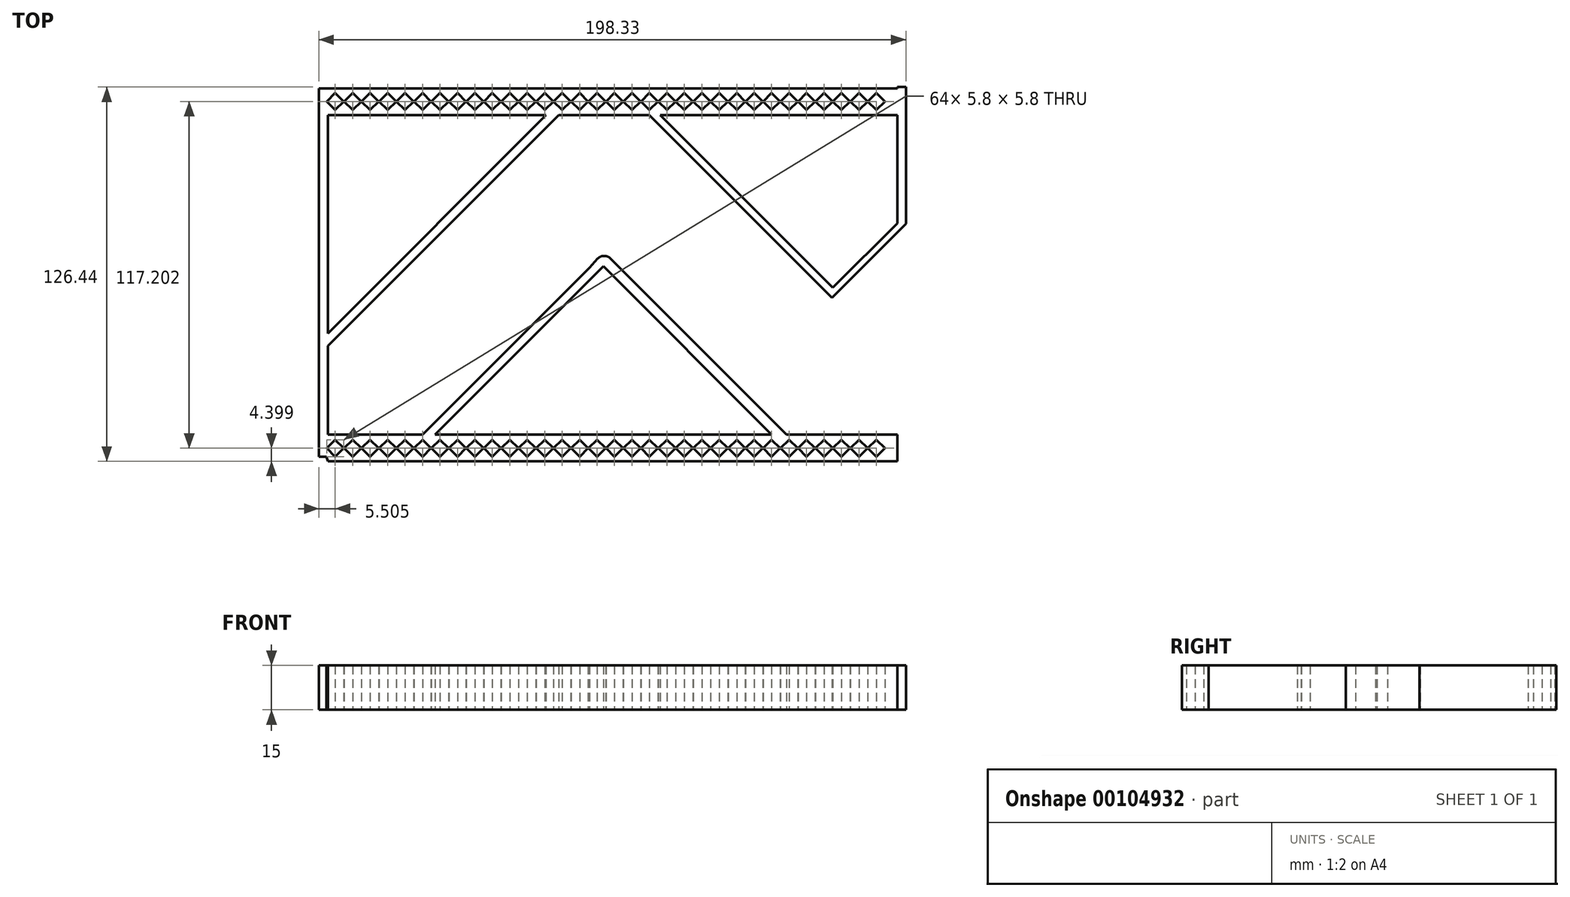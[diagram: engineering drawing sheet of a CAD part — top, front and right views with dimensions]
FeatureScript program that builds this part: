
annotation { "Feature Type Name" : "Feature", "Feature Type Description" : "" }
export const myFeature = defineFeature(function(context is Context, id is Id, definition is map)
    precondition{}
    {
        {
            var Q0;
            Q0=qCreatedBy(makeId("Top.planeOp"),FACE);
            var sketch = newSketch(context, id + "F0", { "sketchPlane" : qUnion([Q0])});
            skLineSegment(sketch, "E0", {"start": v(2.95, 0) * mm, "end": v(0.05, 2.9) * mm});
            skLineSegment(sketch, "E1", {"start": v(0.05, 2.9) * mm, "end": v(2.95, 5.8) * mm});
            skLineSegment(sketch, "E2", {"start": v(2.95, 5.8) * mm, "end": v(5.85, 2.9) * mm});
            skLineSegment(sketch, "E3", {"start": v(5.85, 2.9) * mm, "end": v(2.95, 0) * mm});
            skLineSegment(sketch, "E4", {"start": v(0, 0) * mm, "end": v(0, 5.85) * mm});
            skLineSegment(sketch, "E5.MirrorCS", {"start": v(-2.95, 0) * mm, "end": v(-0.05, 2.9) * mm});
            skLineSegment(sketch, "E6.MirrorCS", {"start": v(-0.05, 2.9) * mm, "end": v(-2.95, 5.8) * mm});
            skLineSegment(sketch, "E7.MirrorCS", {"start": v(-2.95, 5.8) * mm, "end": v(-5.85, 2.9) * mm});
            skLineSegment(sketch, "E8.MirrorCS", {"start": v(-5.85, 2.9) * mm, "end": v(-2.95, 0) * mm});
            skLineSegment(sketch, "E9", {"start": v(5.9, 0) * mm, "end": v(5.9, 5.85) * mm});
            skLineSegment(sketch, "E10", {"start": v(-5.9, 0) * mm, "end": v(-5.9, 6.46) * mm});
            skLineSegment(sketch, "E11.MirrorCS", {"start": v(5.95, 2.9) * mm, "end": v(8.85, 0) * mm});
            skLineSegment(sketch, "E12.MirrorCS", {"start": v(8.85, 5.8) * mm, "end": v(5.95, 2.9) * mm});
            skLineSegment(sketch, "E13.MirrorCS", {"start": v(11.75, 2.9) * mm, "end": v(8.85, 5.8) * mm});
            skLineSegment(sketch, "E14.MirrorCS", {"start": v(8.85, 0) * mm, "end": v(11.75, 2.9) * mm});
            skLineSegment(sketch, "E15.MirrorCS", {"start": v(14.75, 0) * mm, "end": v(11.85, 2.9) * mm});
            skLineSegment(sketch, "E16.MirrorCS", {"start": v(17.64, 2.9) * mm, "end": v(14.75, 0) * mm});
            skLineSegment(sketch, "E17.MirrorCS", {"start": v(14.75, 5.8) * mm, "end": v(17.64, 2.9) * mm});
            skLineSegment(sketch, "E18.MirrorCS", {"start": v(11.85, 2.9) * mm, "end": v(14.75, 5.8) * mm});
            skLineSegment(sketch, "E19.MirrorCS", {"start": v(17.7, 0) * mm, "end": v(17.7, 6.46) * mm});
            skLineSegment(sketch, "E20.MirrorCS", {"start": v(-5.95, 2.9) * mm, "end": v(-8.85, 0) * mm});
            skLineSegment(sketch, "E21.MirrorCS", {"start": v(-8.85, 5.8) * mm, "end": v(-5.95, 2.9) * mm});
            skLineSegment(sketch, "E22.MirrorCS", {"start": v(-11.75, 2.9) * mm, "end": v(-8.85, 5.8) * mm});
            skLineSegment(sketch, "E23.MirrorCS", {"start": v(-8.85, 0) * mm, "end": v(-11.75, 2.9) * mm});
            skLineSegment(sketch, "E24.MirrorCS", {"start": v(-11.85, 2.9) * mm, "end": v(-14.75, 5.8) * mm});
            skLineSegment(sketch, "E25.MirrorCS", {"start": v(-14.75, 5.8) * mm, "end": v(-17.64, 2.9) * mm});
            skLineSegment(sketch, "E26.MirrorCS", {"start": v(-17.64, 2.9) * mm, "end": v(-14.75, 0) * mm});
            skLineSegment(sketch, "E27.MirrorCS", {"start": v(-14.75, 0) * mm, "end": v(-11.85, 2.9) * mm});
            skLineSegment(sketch, "E28.MirrorCS", {"start": v(-20.64, 5.8) * mm, "end": v(-17.74, 2.9) * mm});
            skLineSegment(sketch, "E29.MirrorCS", {"start": v(-23.54, 2.9) * mm, "end": v(-20.64, 5.8) * mm});
            skLineSegment(sketch, "E30.MirrorCS", {"start": v(-20.64, 0) * mm, "end": v(-23.54, 2.9) * mm});
            skLineSegment(sketch, "E31.MirrorCS", {"start": v(-17.74, 2.9) * mm, "end": v(-20.64, 0) * mm});
            skLineSegment(sketch, "E32.MirrorCS", {"start": v(-23.64, 2.9) * mm, "end": v(-26.54, 5.8) * mm});
            skLineSegment(sketch, "E33.MirrorCS", {"start": v(-26.54, 5.8) * mm, "end": v(-29.44, 2.9) * mm});
            skLineSegment(sketch, "E34.MirrorCS", {"start": v(-29.44, 2.9) * mm, "end": v(-26.54, 0) * mm});
            skLineSegment(sketch, "E35.MirrorCS", {"start": v(-26.54, 0) * mm, "end": v(-23.64, 2.9) * mm});
            skLineSegment(sketch, "E36.MirrorCS", {"start": v(-29.5, 0) * mm, "end": v(-29.5, 6.46) * mm});
            skLineSegment(sketch, "E37.MirrorCS", {"start": v(20.64, 5.8) * mm, "end": v(17.74, 2.9) * mm});
            skLineSegment(sketch, "E38.MirrorCS", {"start": v(17.74, 2.9) * mm, "end": v(20.64, 0) * mm});
            skLineSegment(sketch, "E39.MirrorCS", {"start": v(20.64, 0) * mm, "end": v(23.54, 2.9) * mm});
            skLineSegment(sketch, "E40.MirrorCS", {"start": v(23.54, 2.9) * mm, "end": v(20.64, 5.8) * mm});
            skLineSegment(sketch, "E41.MirrorCS", {"start": v(23.64, 2.9) * mm, "end": v(26.54, 5.8) * mm});
            skLineSegment(sketch, "E42.MirrorCS", {"start": v(26.54, 0) * mm, "end": v(23.64, 2.9) * mm});
            skLineSegment(sketch, "E43.MirrorCS", {"start": v(29.44, 2.9) * mm, "end": v(26.54, 0) * mm});
            skLineSegment(sketch, "E44.MirrorCS", {"start": v(26.54, 5.8) * mm, "end": v(29.44, 2.9) * mm});
            skLineSegment(sketch, "E45.MirrorCS", {"start": v(29.54, 2.9) * mm, "end": v(32.44, 0) * mm});
            skLineSegment(sketch, "E46.MirrorCS", {"start": v(32.44, 0) * mm, "end": v(35.34, 2.9) * mm});
            skLineSegment(sketch, "E47.MirrorCS", {"start": v(35.34, 2.9) * mm, "end": v(32.44, 5.8) * mm});
            skLineSegment(sketch, "E48.MirrorCS", {"start": v(32.44, 5.8) * mm, "end": v(29.54, 2.9) * mm});
            skLineSegment(sketch, "E49.MirrorCS", {"start": v(38.34, 0) * mm, "end": v(35.44, 2.9) * mm});
            skLineSegment(sketch, "E50.MirrorCS", {"start": v(41.24, 2.9) * mm, "end": v(38.34, 0) * mm});
            skLineSegment(sketch, "E51.MirrorCS", {"start": v(38.34, 5.8) * mm, "end": v(41.24, 2.9) * mm});
            skLineSegment(sketch, "E52.MirrorCS", {"start": v(35.44, 2.9) * mm, "end": v(38.34, 5.8) * mm});
            skLineSegment(sketch, "E53.MirrorCS", {"start": v(41.34, 2.9) * mm, "end": v(44.24, 0) * mm});
            skLineSegment(sketch, "E54.MirrorCS", {"start": v(44.24, 0) * mm, "end": v(47.14, 2.9) * mm});
            skLineSegment(sketch, "E55.MirrorCS", {"start": v(47.14, 2.9) * mm, "end": v(44.24, 5.8) * mm});
            skLineSegment(sketch, "E56.MirrorCS", {"start": v(44.24, 5.8) * mm, "end": v(41.34, 2.9) * mm});
            skLineSegment(sketch, "E57.MirrorCS", {"start": v(50.14, 0) * mm, "end": v(47.24, 2.9) * mm});
            skLineSegment(sketch, "E58.MirrorCS", {"start": v(53.03, 2.9) * mm, "end": v(50.14, 0) * mm});
            skLineSegment(sketch, "E59.MirrorCS", {"start": v(50.14, 5.8) * mm, "end": v(53.03, 2.9) * mm});
            skLineSegment(sketch, "E60.MirrorCS", {"start": v(47.24, 2.9) * mm, "end": v(50.14, 5.8) * mm});
            skLineSegment(sketch, "E61.MirrorCS", {"start": v(53.13, 2.9) * mm, "end": v(56.03, 0) * mm});
            skLineSegment(sketch, "E62.MirrorCS", {"start": v(56.03, 0) * mm, "end": v(58.93, 2.9) * mm});
            skLineSegment(sketch, "E63.MirrorCS", {"start": v(58.93, 2.9) * mm, "end": v(56.03, 5.8) * mm});
            skLineSegment(sketch, "E64.MirrorCS", {"start": v(56.03, 5.8) * mm, "end": v(53.13, 2.9) * mm});
            skLineSegment(sketch, "E65.MirrorCS", {"start": v(61.93, 0) * mm, "end": v(59.03, 2.9) * mm});
            skLineSegment(sketch, "E66.MirrorCS", {"start": v(64.83, 2.9) * mm, "end": v(61.93, 0) * mm});
            skLineSegment(sketch, "E67.MirrorCS", {"start": v(61.93, 5.8) * mm, "end": v(64.83, 2.9) * mm});
            skLineSegment(sketch, "E68.MirrorCS", {"start": v(59.03, 2.9) * mm, "end": v(61.93, 5.8) * mm});
            skLineSegment(sketch, "E69.MirrorCS", {"start": v(64.88, 0) * mm, "end": v(64.88, 6.46) * mm});
            skLineSegment(sketch, "E70.MirrorCS", {"start": v(-32.44, 5.8) * mm, "end": v(-29.54, 2.9) * mm});
            skLineSegment(sketch, "E71.MirrorCS", {"start": v(-35.34, 2.9) * mm, "end": v(-32.44, 5.8) * mm});
            skLineSegment(sketch, "E72.MirrorCS", {"start": v(-32.44, 0) * mm, "end": v(-35.34, 2.9) * mm});
            skLineSegment(sketch, "E73.MirrorCS", {"start": v(-29.54, 2.9) * mm, "end": v(-32.44, 0) * mm});
            skLineSegment(sketch, "E74.MirrorCS", {"start": v(-35.44, 2.9) * mm, "end": v(-38.34, 5.8) * mm});
            skLineSegment(sketch, "E75.MirrorCS", {"start": v(-38.34, 5.8) * mm, "end": v(-41.24, 2.9) * mm});
            skLineSegment(sketch, "E76.MirrorCS", {"start": v(-38.34, 0) * mm, "end": v(-35.44, 2.9) * mm});
            skLineSegment(sketch, "E77.MirrorCS", {"start": v(-41.24, 2.9) * mm, "end": v(-38.34, 0) * mm});
            skLineSegment(sketch, "E78.MirrorCS", {"start": v(-44.24, 5.8) * mm, "end": v(-41.34, 2.9) * mm});
            skLineSegment(sketch, "E79.MirrorCS", {"start": v(-47.14, 2.9) * mm, "end": v(-44.24, 5.8) * mm});
            skLineSegment(sketch, "E80.MirrorCS", {"start": v(-44.24, 0) * mm, "end": v(-47.14, 2.9) * mm});
            skLineSegment(sketch, "E81.MirrorCS", {"start": v(-41.34, 2.9) * mm, "end": v(-44.24, 0) * mm});
            skLineSegment(sketch, "E82.MirrorCS", {"start": v(-47.24, 2.9) * mm, "end": v(-50.14, 5.8) * mm});
            skLineSegment(sketch, "E83.MirrorCS", {"start": v(-50.14, 5.8) * mm, "end": v(-53.03, 2.9) * mm});
            skLineSegment(sketch, "E84.MirrorCS", {"start": v(-53.03, 2.9) * mm, "end": v(-50.14, 0) * mm});
            skLineSegment(sketch, "E85.MirrorCS", {"start": v(-50.14, 0) * mm, "end": v(-47.24, 2.9) * mm});
            skLineSegment(sketch, "E86.MirrorCS", {"start": v(-56.03, 5.8) * mm, "end": v(-53.13, 2.9) * mm});
            skLineSegment(sketch, "E87.MirrorCS", {"start": v(-58.93, 2.9) * mm, "end": v(-56.03, 5.8) * mm});
            skLineSegment(sketch, "E88.MirrorCS", {"start": v(-56.03, 0) * mm, "end": v(-58.93, 2.9) * mm});
            skLineSegment(sketch, "E89.MirrorCS", {"start": v(-53.13, 2.9) * mm, "end": v(-56.03, 0) * mm});
            skLineSegment(sketch, "E90.MirrorCS", {"start": v(-59.03, 2.9) * mm, "end": v(-61.93, 5.8) * mm});
            skLineSegment(sketch, "E91.MirrorCS", {"start": v(-61.93, 5.8) * mm, "end": v(-64.83, 2.9) * mm});
            skLineSegment(sketch, "E92.MirrorCS", {"start": v(-64.83, 2.9) * mm, "end": v(-61.93, 0) * mm});
            skLineSegment(sketch, "E93.MirrorCS", {"start": v(-61.93, 0) * mm, "end": v(-59.03, 2.9) * mm});
            skLineSegment(sketch, "E94.MirrorCS", {"start": v(-67.83, 5.8) * mm, "end": v(-64.93, 2.9) * mm});
            skLineSegment(sketch, "E95.MirrorCS", {"start": v(-70.73, 2.9) * mm, "end": v(-67.83, 5.8) * mm});
            skLineSegment(sketch, "E96.MirrorCS", {"start": v(-67.83, 0) * mm, "end": v(-70.73, 2.9) * mm});
            skLineSegment(sketch, "E97.MirrorCS", {"start": v(-64.93, 2.9) * mm, "end": v(-67.83, 0) * mm});
            skLineSegment(sketch, "E98.MirrorCS", {"start": v(-70.83, 2.9) * mm, "end": v(-73.73, 5.8) * mm});
            skLineSegment(sketch, "E99.MirrorCS", {"start": v(-73.73, 5.8) * mm, "end": v(-76.63, 2.9) * mm});
            skLineSegment(sketch, "E100.MirrorCS", {"start": v(-76.63, 2.9) * mm, "end": v(-73.73, 0) * mm});
            skLineSegment(sketch, "E101.MirrorCS", {"start": v(-73.73, 0) * mm, "end": v(-70.83, 2.9) * mm});
            skLineSegment(sketch, "E102.MirrorCS", {"start": v(-79.63, 5.8) * mm, "end": v(-76.73, 2.9) * mm});
            skLineSegment(sketch, "E103.MirrorCS", {"start": v(-82.53, 2.9) * mm, "end": v(-79.63, 5.8) * mm});
            skLineSegment(sketch, "E104.MirrorCS", {"start": v(-79.63, 0) * mm, "end": v(-82.53, 2.9) * mm});
            skLineSegment(sketch, "E105.MirrorCS", {"start": v(-76.73, 2.9) * mm, "end": v(-79.63, 0) * mm});
            skLineSegment(sketch, "E106.MirrorCS", {"start": v(-82.63, 2.9) * mm, "end": v(-85.52, 5.8) * mm});
            skLineSegment(sketch, "E107.MirrorCS", {"start": v(-85.52, 5.8) * mm, "end": v(-88.42, 2.9) * mm});
            skLineSegment(sketch, "E108.MirrorCS", {"start": v(-88.42, 2.9) * mm, "end": v(-85.52, 0) * mm});
            skLineSegment(sketch, "E109.MirrorCS", {"start": v(-85.52, 0) * mm, "end": v(-82.63, 2.9) * mm});
            skLineSegment(sketch, "E110.MirrorCS", {"start": v(-91.42, 5.8) * mm, "end": v(-88.52, 2.9) * mm});
            skLineSegment(sketch, "E111.MirrorCS", {"start": v(-94.32, 2.9) * mm, "end": v(-91.42, 5.8) * mm});
            skLineSegment(sketch, "E112.MirrorCS", {"start": v(-91.42, 0) * mm, "end": v(-94.32, 2.9) * mm});
            skLineSegment(sketch, "E113.MirrorCS", {"start": v(-88.52, 2.9) * mm, "end": v(-91.42, 0) * mm});
            skLineSegment(sketch, "E114.MirrorCS", {"start": v(-94.42, 2.9) * mm, "end": v(-97.32, 5.8) * mm});
            skLineSegment(sketch, "E115.MirrorCS", {"start": v(-97.32, 5.8) * mm, "end": v(-100.22, 2.9) * mm});
            skLineSegment(sketch, "E116.MirrorCS", {"start": v(-100.22, 2.9) * mm, "end": v(-97.32, 0) * mm});
            skLineSegment(sketch, "E117.MirrorCS", {"start": v(-97.32, 0) * mm, "end": v(-94.42, 2.9) * mm});
            skLineSegment(sketch, "E118.MirrorCS", {"start": v(-115.02, 5.8) * mm, "end": v(-112.12, 2.9) * mm});
            skLineSegment(sketch, "E119.MirrorCS", {"start": v(-120.91, 0) * mm, "end": v(-118.02, 2.9) * mm});
            skLineSegment(sketch, "E120.MirrorCS", {"start": v(-106.12, 2.9) * mm, "end": v(-103.22, 5.8) * mm});
            skLineSegment(sketch, "E121.MirrorCS", {"start": v(-117.92, 2.9) * mm, "end": v(-115.02, 5.8) * mm});
            skLineSegment(sketch, "E122.MirrorCS", {"start": v(-109.12, 0) * mm, "end": v(-106.22, 2.9) * mm});
            skLineSegment(sketch, "E123.MirrorCS", {"start": v(-123.81, 2.9) * mm, "end": v(-120.91, 0) * mm});
            skLineSegment(sketch, "E124.MirrorCS", {"start": v(-103.22, 0) * mm, "end": v(-106.12, 2.9) * mm});
            skLineSegment(sketch, "E125.MirrorCS", {"start": v(-109.12, 5.8) * mm, "end": v(-112.02, 2.9) * mm});
            skLineSegment(sketch, "E126.MirrorCS", {"start": v(-115.02, 0) * mm, "end": v(-117.92, 2.9) * mm});
            skLineSegment(sketch, "E127.MirrorCS", {"start": v(-118.02, 2.9) * mm, "end": v(-120.91, 5.8) * mm});
            skLineSegment(sketch, "E128.MirrorCS", {"start": v(-123.86, 0) * mm, "end": v(-123.86, 6.46) * mm});
            skLineSegment(sketch, "E129.MirrorCS", {"start": v(-112.12, 2.9) * mm, "end": v(-115.02, 0) * mm});
            skLineSegment(sketch, "E130.MirrorCS", {"start": v(-120.91, 5.8) * mm, "end": v(-123.81, 2.9) * mm});
            skLineSegment(sketch, "E131.MirrorCS", {"start": v(-106.22, 2.9) * mm, "end": v(-109.12, 5.8) * mm});
            skLineSegment(sketch, "E132.MirrorCS", {"start": v(-112.02, 2.9) * mm, "end": v(-109.12, 0) * mm});
            skLineSegment(sketch, "E133.MirrorCS", {"start": v(-76.68, 0) * mm, "end": v(-76.68, 6.46) * mm});
            skLineSegment(sketch, "E134.MirrorCS", {"start": v(-100.32, 2.9) * mm, "end": v(-103.22, 0) * mm});
            skLineSegment(sketch, "E135.MirrorCS", {"start": v(-103.22, 5.8) * mm, "end": v(-100.32, 2.9) * mm});
            skLineSegment(sketch, "E136.bottom", {"start": v(-123.42, -1.5) * mm, "end": v(68.98, -1.5) * mm});
            skLineSegment(sketch, "E136.top", {"start": v(-123.42, 7.5) * mm, "end": v(68.98, 7.5) * mm});
            skLineSegment(sketch, "E136.right", {"start": v(68.98, -1.5) * mm, "end": v(68.98, 7.5) * mm});
            skCircle(sketch, "E137", {"center": v(-103.92, 28.34) * mm, "radius": 19 * mm});
            skLineSegment(sketch, "E138", {"start": v(-123.42, 7.5) * mm, "end": v(-123.42, 37.5) * mm});
            skLineSegment(sketch, "E139", {"start": v(-123.42, 37.5) * mm, "end": v(-45.42, 115.5) * mm});
            skLineSegment(sketch, "E140", {"start": v(-139.2, 61.5) * mm, "end": v(93.37, 61.5) * mm, "construction": true});
            skLineSegment(sketch, "E141.MirrorCS", {"start": v(-82.63, 120.1) * mm, "end": v(-85.52, 117.2) * mm});
            skLineSegment(sketch, "E142.MirrorCS", {"start": v(-88.42, 120.1) * mm, "end": v(-85.52, 123) * mm});
            skLineSegment(sketch, "E143.MirrorCS", {"start": v(-85.52, 117.2) * mm, "end": v(-88.42, 120.1) * mm});
            skLineSegment(sketch, "E144.MirrorCS", {"start": v(-85.52, 123) * mm, "end": v(-82.63, 120.1) * mm});
            skLineSegment(sketch, "E145.MirrorCS", {"start": v(-91.42, 117.2) * mm, "end": v(-88.52, 120.1) * mm});
            skLineSegment(sketch, "E146.MirrorCS", {"start": v(-88.52, 120.1) * mm, "end": v(-91.42, 123) * mm});
            skLineSegment(sketch, "E147.MirrorCS", {"start": v(-79.63, 123) * mm, "end": v(-82.53, 120.1) * mm});
            skLineSegment(sketch, "E148.MirrorCS", {"start": v(-82.53, 120.1) * mm, "end": v(-79.63, 117.2) * mm});
            skLineSegment(sketch, "E149.MirrorCS", {"start": v(-94.32, 120.1) * mm, "end": v(-91.42, 117.2) * mm});
            skLineSegment(sketch, "E150.MirrorCS", {"start": v(-97.32, 123) * mm, "end": v(-94.42, 120.1) * mm});
            skLineSegment(sketch, "E151.MirrorCS", {"start": v(-115.02, 123) * mm, "end": v(-117.92, 120.1) * mm});
            skLineSegment(sketch, "E152.MirrorCS", {"start": v(-120.91, 123) * mm, "end": v(-118.02, 120.1) * mm});
            skLineSegment(sketch, "E153.MirrorCS", {"start": v(-118.02, 120.1) * mm, "end": v(-120.91, 117.2) * mm});
            skLineSegment(sketch, "E154.MirrorCS", {"start": v(-91.42, 123) * mm, "end": v(-94.32, 120.1) * mm});
            skLineSegment(sketch, "E155.MirrorCS", {"start": v(-117.92, 120.1) * mm, "end": v(-115.02, 117.2) * mm});
            skLineSegment(sketch, "E156.MirrorCS", {"start": v(-94.42, 120.1) * mm, "end": v(-97.32, 117.2) * mm});
            skLineSegment(sketch, "E157.MirrorCS", {"start": v(-109.12, 117.2) * mm, "end": v(-112.02, 120.1) * mm});
            skLineSegment(sketch, "E158.MirrorCS", {"start": v(-112.02, 120.1) * mm, "end": v(-109.12, 123) * mm});
            skLineSegment(sketch, "E159.MirrorCS", {"start": v(-109.12, 123) * mm, "end": v(-106.22, 120.1) * mm});
            skLineSegment(sketch, "E160.MirrorCS", {"start": v(-115.02, 117.2) * mm, "end": v(-112.12, 120.1) * mm});
            skLineSegment(sketch, "E161.MirrorCS", {"start": v(-103.22, 123) * mm, "end": v(-106.12, 120.1) * mm});
            skLineSegment(sketch, "E162.MirrorCS", {"start": v(-106.12, 120.1) * mm, "end": v(-103.22, 117.2) * mm});
            skLineSegment(sketch, "E163.MirrorCS", {"start": v(-106.22, 120.1) * mm, "end": v(-109.12, 117.2) * mm});
            skLineSegment(sketch, "E164.MirrorCS", {"start": v(-112.12, 120.1) * mm, "end": v(-115.02, 123) * mm});
            skLineSegment(sketch, "E165.MirrorCS", {"start": v(-97.32, 117.2) * mm, "end": v(-100.22, 120.1) * mm});
            skLineSegment(sketch, "E166.MirrorCS", {"start": v(-76.73, 120.1) * mm, "end": v(-79.63, 123) * mm});
            skLineSegment(sketch, "E167.MirrorCS", {"start": v(-100.22, 120.1) * mm, "end": v(-97.32, 123) * mm});
            skLineSegment(sketch, "E168.MirrorCS", {"start": v(-79.63, 117.2) * mm, "end": v(-76.73, 120.1) * mm});
            skLineSegment(sketch, "E169.MirrorCS", {"start": v(-123.81, 120.1) * mm, "end": v(-120.91, 123) * mm});
            skLineSegment(sketch, "E170.MirrorCS", {"start": v(-73.73, 117.2) * mm, "end": v(-76.63, 120.1) * mm});
            skLineSegment(sketch, "E171.MirrorCS", {"start": v(-100.32, 120.1) * mm, "end": v(-103.22, 123) * mm});
            skLineSegment(sketch, "E172.MirrorCS", {"start": v(38.34, 123) * mm, "end": v(35.44, 120.1) * mm});
            skLineSegment(sketch, "E173.MirrorCS", {"start": v(-76.63, 120.1) * mm, "end": v(-73.73, 123) * mm});
            skLineSegment(sketch, "E174.MirrorCS", {"start": v(-103.22, 117.2) * mm, "end": v(-100.32, 120.1) * mm});
            skLineSegment(sketch, "E175.MirrorCS", {"start": v(-120.91, 117.2) * mm, "end": v(-123.81, 120.1) * mm});
            skLineSegment(sketch, "E176.MirrorCS", {"start": v(-76.68, 123) * mm, "end": v(-76.68, 116.54) * mm});
            skLineSegment(sketch, "E177.MirrorCS", {"start": v(23.64, 120.1) * mm, "end": v(26.54, 117.2) * mm});
            skLineSegment(sketch, "E178.MirrorCS", {"start": v(-26.54, 117.2) * mm, "end": v(-29.44, 120.1) * mm});
            skLineSegment(sketch, "E179.MirrorCS", {"start": v(35.34, 120.1) * mm, "end": v(32.44, 117.2) * mm});
            skLineSegment(sketch, "E180.MirrorCS", {"start": v(32.44, 117.2) * mm, "end": v(29.54, 120.1) * mm});
            skLineSegment(sketch, "E181.MirrorCS", {"start": v(8.85, 117.2) * mm, "end": v(5.95, 120.1) * mm});
            skLineSegment(sketch, "E182.MirrorCS", {"start": v(5.95, 120.1) * mm, "end": v(8.85, 123) * mm});
            skLineSegment(sketch, "E183.MirrorCS", {"start": v(-29.5, 123) * mm, "end": v(-29.5, 116.54) * mm});
            skLineSegment(sketch, "E184.MirrorCS", {"start": v(-70.83, 120.1) * mm, "end": v(-73.73, 117.2) * mm});
            skLineSegment(sketch, "E185.MirrorCS", {"start": v(11.85, 120.1) * mm, "end": v(14.75, 117.2) * mm});
            skLineSegment(sketch, "E186.MirrorCS", {"start": v(5.9, 123) * mm, "end": v(5.9, 117.15) * mm});
            skLineSegment(sketch, "E187.MirrorCS", {"start": v(-2.95, 117.2) * mm, "end": v(-5.85, 120.1) * mm});
            skLineSegment(sketch, "E188.MirrorCS", {"start": v(35.44, 120.1) * mm, "end": v(38.34, 117.2) * mm});
            skLineSegment(sketch, "E189.MirrorCS", {"start": v(-0.05, 120.1) * mm, "end": v(-2.95, 117.2) * mm});
            skLineSegment(sketch, "E190.MirrorCS", {"start": v(-2.95, 123) * mm, "end": v(-0.05, 120.1) * mm});
            skLineSegment(sketch, "E191.MirrorCS", {"start": v(0, 123) * mm, "end": v(0, 117.15) * mm});
            skLineSegment(sketch, "E192.MirrorCS", {"start": v(-29.54, 120.1) * mm, "end": v(-32.44, 123) * mm});
            skLineSegment(sketch, "E193.MirrorCS", {"start": v(5.85, 120.1) * mm, "end": v(2.95, 123) * mm});
            skLineSegment(sketch, "E194.MirrorCS", {"start": v(2.95, 117.2) * mm, "end": v(5.85, 120.1) * mm});
            skLineSegment(sketch, "E195.MirrorCS", {"start": v(0.05, 120.1) * mm, "end": v(2.95, 117.2) * mm});
            skLineSegment(sketch, "E196.MirrorCS", {"start": v(29.44, 120.1) * mm, "end": v(26.54, 123) * mm});
            skLineSegment(sketch, "E197.MirrorCS", {"start": v(2.95, 123) * mm, "end": v(0.05, 120.1) * mm});
            skLineSegment(sketch, "E198.MirrorCS", {"start": v(14.75, 123) * mm, "end": v(11.85, 120.1) * mm});
            skLineSegment(sketch, "E199.MirrorCS", {"start": v(8.85, 123) * mm, "end": v(11.75, 120.1) * mm});
            skLineSegment(sketch, "E200.MirrorCS", {"start": v(11.75, 120.1) * mm, "end": v(8.85, 117.2) * mm});
            skLineSegment(sketch, "E201.MirrorCS", {"start": v(26.54, 117.2) * mm, "end": v(29.44, 120.1) * mm});
            skLineSegment(sketch, "E202.MirrorCS", {"start": v(-123.86, 123) * mm, "end": v(-123.86, 116.54) * mm});
            skLineSegment(sketch, "E203.MirrorCS", {"start": v(32.44, 123) * mm, "end": v(35.34, 120.1) * mm});
            skLineSegment(sketch, "E204.MirrorCS", {"start": v(29.54, 120.1) * mm, "end": v(32.44, 123) * mm});
            skLineSegment(sketch, "E205.MirrorCS", {"start": v(20.64, 123) * mm, "end": v(23.54, 120.1) * mm});
            skLineSegment(sketch, "E206.MirrorCS", {"start": v(-29.44, 120.1) * mm, "end": v(-26.54, 123) * mm});
            skLineSegment(sketch, "E207.MirrorCS", {"start": v(-32.44, 117.2) * mm, "end": v(-29.54, 120.1) * mm});
            skLineSegment(sketch, "E208.MirrorCS", {"start": v(23.54, 120.1) * mm, "end": v(20.64, 117.2) * mm});
            skLineSegment(sketch, "E209.MirrorCS", {"start": v(-73.73, 123) * mm, "end": v(-70.83, 120.1) * mm});
            skLineSegment(sketch, "E210.MirrorCS", {"start": v(26.54, 123) * mm, "end": v(23.64, 120.1) * mm});
            skLineSegment(sketch, "E211.MirrorCS", {"start": v(-67.83, 123) * mm, "end": v(-70.73, 120.1) * mm});
            skLineSegment(sketch, "E212.MirrorCS", {"start": v(56.03, 117.2) * mm, "end": v(53.13, 120.1) * mm});
            skLineSegment(sketch, "E213.MirrorCS", {"start": v(-44.24, 123) * mm, "end": v(-47.14, 120.1) * mm});
            skLineSegment(sketch, "E214.MirrorCS", {"start": v(-70.73, 120.1) * mm, "end": v(-67.83, 117.2) * mm});
            skLineSegment(sketch, "E215.MirrorCS", {"start": v(17.7, 123) * mm, "end": v(17.7, 116.54) * mm});
            skLineSegment(sketch, "E216.MirrorCS", {"start": v(-41.34, 120.1) * mm, "end": v(-44.24, 123) * mm});
            skLineSegment(sketch, "E217.MirrorCS", {"start": v(61.93, 123) * mm, "end": v(59.03, 120.1) * mm});
            skLineSegment(sketch, "E218.MirrorCS", {"start": v(41.24, 120.1) * mm, "end": v(38.34, 123) * mm});
            skLineSegment(sketch, "E219.MirrorCS", {"start": v(-26.54, 123) * mm, "end": v(-23.64, 120.1) * mm});
            skLineSegment(sketch, "E220.MirrorCS", {"start": v(-64.93, 120.1) * mm, "end": v(-67.83, 123) * mm});
            skLineSegment(sketch, "E221.MirrorCS", {"start": v(-23.64, 120.1) * mm, "end": v(-26.54, 117.2) * mm});
            skLineSegment(sketch, "E222.MirrorCS", {"start": v(56.03, 123) * mm, "end": v(58.93, 120.1) * mm});
            skLineSegment(sketch, "E223.MirrorCS", {"start": v(-44.24, 117.2) * mm, "end": v(-41.34, 120.1) * mm});
            skLineSegment(sketch, "E224.MirrorCS", {"start": v(17.64, 120.1) * mm, "end": v(14.75, 123) * mm});
            skLineSegment(sketch, "E225.MirrorCS", {"start": v(58.93, 120.1) * mm, "end": v(56.03, 117.2) * mm});
            skLineSegment(sketch, "E226.MirrorCS", {"start": v(-67.83, 117.2) * mm, "end": v(-64.93, 120.1) * mm});
            skLineSegment(sketch, "E227.MirrorCS", {"start": v(-5.95, 120.1) * mm, "end": v(-8.85, 123) * mm});
            skLineSegment(sketch, "E228.MirrorCS", {"start": v(-47.24, 120.1) * mm, "end": v(-50.14, 117.2) * mm});
            skLineSegment(sketch, "E229.MirrorCS", {"start": v(64.83, 120.1) * mm, "end": v(61.93, 123) * mm});
            skLineSegment(sketch, "E230.MirrorCS", {"start": v(38.34, 117.2) * mm, "end": v(41.24, 120.1) * mm});
            skLineSegment(sketch, "E231.MirrorCS", {"start": v(-5.9, 123) * mm, "end": v(-5.9, 116.54) * mm});
            skLineSegment(sketch, "E232.MirrorCS", {"start": v(-61.93, 117.2) * mm, "end": v(-64.83, 120.1) * mm});
            skLineSegment(sketch, "E233.MirrorCS", {"start": v(-8.85, 117.2) * mm, "end": v(-5.95, 120.1) * mm});
            skLineSegment(sketch, "E234.MirrorCS", {"start": v(-5.85, 120.1) * mm, "end": v(-2.95, 123) * mm});
            skLineSegment(sketch, "E235.MirrorCS", {"start": v(-50.14, 117.2) * mm, "end": v(-53.03, 120.1) * mm});
            skLineSegment(sketch, "E236.MirrorCS", {"start": v(20.64, 117.2) * mm, "end": v(17.74, 120.1) * mm});
            skLineSegment(sketch, "E237.MirrorCS", {"start": v(-23.54, 120.1) * mm, "end": v(-20.64, 117.2) * mm});
            skLineSegment(sketch, "E238.MirrorCS", {"start": v(50.14, 117.2) * mm, "end": v(53.03, 120.1) * mm});
            skLineSegment(sketch, "E239.MirrorCS", {"start": v(-38.34, 117.2) * mm, "end": v(-41.24, 120.1) * mm});
            skLineSegment(sketch, "E240.MirrorCS", {"start": v(-47.14, 120.1) * mm, "end": v(-44.24, 117.2) * mm});
            skLineSegment(sketch, "E241.MirrorCS", {"start": v(-53.13, 120.1) * mm, "end": v(-56.03, 123) * mm});
            skLineSegment(sketch, "E242.MirrorCS", {"start": v(-14.75, 123) * mm, "end": v(-11.85, 120.1) * mm});
            skLineSegment(sketch, "E243.MirrorCS", {"start": v(-11.75, 120.1) * mm, "end": v(-8.85, 117.2) * mm});
            skLineSegment(sketch, "E244.MirrorCS", {"start": v(-20.64, 117.2) * mm, "end": v(-17.74, 120.1) * mm});
            skLineSegment(sketch, "E245.MirrorCS", {"start": v(53.03, 120.1) * mm, "end": v(50.14, 123) * mm});
            skLineSegment(sketch, "E246.MirrorCS", {"start": v(-53.03, 120.1) * mm, "end": v(-50.14, 123) * mm});
            skLineSegment(sketch, "E247.MirrorCS", {"start": v(59.03, 120.1) * mm, "end": v(61.93, 117.2) * mm});
            skLineSegment(sketch, "E248.MirrorCS", {"start": v(17.74, 120.1) * mm, "end": v(20.64, 123) * mm});
            skLineSegment(sketch, "E249.MirrorCS", {"start": v(-61.93, 123) * mm, "end": v(-59.03, 120.1) * mm});
            skLineSegment(sketch, "E250.MirrorCS", {"start": v(-59.03, 120.1) * mm, "end": v(-61.93, 117.2) * mm});
            skLineSegment(sketch, "E251.MirrorCS", {"start": v(-35.44, 120.1) * mm, "end": v(-38.34, 117.2) * mm});
            skLineSegment(sketch, "E252.MirrorCS", {"start": v(-64.83, 120.1) * mm, "end": v(-61.93, 123) * mm});
            skLineSegment(sketch, "E253.MirrorCS", {"start": v(-17.74, 120.1) * mm, "end": v(-20.64, 123) * mm});
            skLineSegment(sketch, "E254.MirrorCS", {"start": v(53.13, 120.1) * mm, "end": v(56.03, 123) * mm});
            skLineSegment(sketch, "E255.MirrorCS", {"start": v(-41.24, 120.1) * mm, "end": v(-38.34, 123) * mm});
            skLineSegment(sketch, "E256.MirrorCS", {"start": v(-38.34, 123) * mm, "end": v(-35.44, 120.1) * mm});
            skLineSegment(sketch, "E257.MirrorCS", {"start": v(14.75, 117.2) * mm, "end": v(17.64, 120.1) * mm});
            skLineSegment(sketch, "E258.MirrorCS", {"start": v(-56.03, 117.2) * mm, "end": v(-53.13, 120.1) * mm});
            skLineSegment(sketch, "E259.MirrorCS", {"start": v(41.34, 120.1) * mm, "end": v(44.24, 123) * mm});
            skLineSegment(sketch, "E260.MirrorCS", {"start": v(-32.44, 123) * mm, "end": v(-35.34, 120.1) * mm});
            skLineSegment(sketch, "E261.MirrorCS", {"start": v(-20.64, 123) * mm, "end": v(-23.54, 120.1) * mm});
            skLineSegment(sketch, "E262.MirrorCS", {"start": v(-56.03, 123) * mm, "end": v(-58.93, 120.1) * mm});
            skLineSegment(sketch, "E263.MirrorCS", {"start": v(-11.85, 120.1) * mm, "end": v(-14.75, 117.2) * mm});
            skLineSegment(sketch, "E264.MirrorCS", {"start": v(-8.85, 123) * mm, "end": v(-11.75, 120.1) * mm});
            skLineSegment(sketch, "E265.MirrorCS", {"start": v(-35.34, 120.1) * mm, "end": v(-32.44, 117.2) * mm});
            skLineSegment(sketch, "E266.MirrorCS", {"start": v(-50.14, 123) * mm, "end": v(-47.24, 120.1) * mm});
            skLineSegment(sketch, "E267.MirrorCS", {"start": v(-58.93, 120.1) * mm, "end": v(-56.03, 117.2) * mm});
            skLineSegment(sketch, "E268.MirrorCS", {"start": v(-17.64, 120.1) * mm, "end": v(-14.75, 123) * mm});
            skLineSegment(sketch, "E269.MirrorCS", {"start": v(-14.75, 117.2) * mm, "end": v(-17.64, 120.1) * mm});
            skLineSegment(sketch, "E270.MirrorCS", {"start": v(44.24, 117.2) * mm, "end": v(41.34, 120.1) * mm});
            skLineSegment(sketch, "E271.MirrorCS", {"start": v(61.93, 117.2) * mm, "end": v(64.83, 120.1) * mm});
            skLineSegment(sketch, "E272.MirrorCS", {"start": v(50.14, 123) * mm, "end": v(47.24, 120.1) * mm});
            skLineSegment(sketch, "E273.MirrorCS", {"start": v(47.24, 120.1) * mm, "end": v(50.14, 117.2) * mm});
            skLineSegment(sketch, "E274.MirrorCS", {"start": v(44.24, 123) * mm, "end": v(47.14, 120.1) * mm});
            skLineSegment(sketch, "E275.MirrorCS", {"start": v(64.88, 123) * mm, "end": v(64.88, 116.54) * mm});
            skLineSegment(sketch, "E276.MirrorCS", {"start": v(47.14, 120.1) * mm, "end": v(44.24, 117.2) * mm});
            skLineSegment(sketch, "E277.MirrorCS", {"start": v(-123.42, 115.5) * mm, "end": v(68.98, 115.5) * mm});
            skLineSegment(sketch, "E278.MirrorCS", {"start": v(-123.42, 124.5) * mm, "end": v(68.98, 124.5) * mm});
            skLineSegment(sketch, "E279.MirrorCS", {"start": v(-123.42, 124.5) * mm, "end": v(-123.42, 115.5) * mm});
            skLineSegment(sketch, "E280.MirrorCS", {"start": v(68.98, 124.5) * mm, "end": v(68.98, 115.5) * mm});
            skCircle(sketch, "E281", {"center": v(-37.55, 96.5) * mm, "radius": 19 * mm});
            skLineSegment(sketch, "E282", {"start": v(-91.42, 7.5) * mm, "end": v(-35.05, 63.87) * mm});
            skLineSegment(sketch, "E283", {"start": v(-14.75, 115.5) * mm, "end": v(46.95, 53.8) * mm});
            skLineSegment(sketch, "E284", {"start": v(31.58, 7.5) * mm, "end": v(-30.16, 69.24) * mm});
            skLineSegment(sketch, "E285", {"start": v(-30.16, 69.24) * mm, "end": v(-35.05, 63.87) * mm});
            skCircle(sketch, "E286", {"center": v(56.42, 26.5) * mm, "radius": 19 * mm});
            skLineSegment(sketch, "E287", {"start": v(46.95, 53.8) * mm, "end": v(82.3, 89.16) * mm});
            skLineSegment(sketch, "E288", {"start": v(-126.42, 42.6) * mm, "end": v(-126.42, 0) * mm});
            skLineSegment(sketch, "E289", {"start": v(-126.42, 0) * mm, "end": v(-123.86, 0) * mm});
            skLineSegment(sketch, "E290", {"start": v(-87.18, 7.5) * mm, "end": v(-33.18, 61.5) * mm});
            skLineSegment(sketch, "E291", {"start": v(68.91, 124.94) * mm, "end": v(71.91, 124.94) * mm});
            skLineSegment(sketch, "E292", {"start": v(-126.42, 38.74) * mm, "end": v(-49.67, 115.5) * mm});
            skLineSegment(sketch, "E293", {"start": v(26.54, 7.5) * mm, "end": v(-30.31, 64.35) * mm});
            skLineSegment(sketch, "E294", {"start": v(-30.31, 64.35) * mm, "end": v(-33.18, 61.5) * mm});
            skLineSegment(sketch, "E295", {"start": v(71.91, 124.94) * mm, "end": v(71.91, 78.76) * mm});
            skLineSegment(sketch, "E296", {"start": v(68.98, 115.5) * mm, "end": v(68.98, 78.95) * mm});
            skLineSegment(sketch, "E297", {"start": v(68.98, 78.95) * mm, "end": v(47.24, 57.2) * mm});
            skLineSegment(sketch, "E298", {"start": v(47.24, 57.2) * mm, "end": v(-11.06, 115.5) * mm});
            skLineSegment(sketch, "E299", {"start": v(-123.42, 124.5) * mm, "end": v(-126.42, 124.5) * mm});
            skLineSegment(sketch, "E300", {"start": v(-126.42, 124.5) * mm, "end": v(-126.42, 38.85) * mm});
            skLineSegment(sketch, "E301", {"start": v(-123.42, 115.5) * mm, "end": v(-123.42, 41.74) * mm});
            skLineSegment(sketch, "E302", {"start": v(-123.42, 37.5) * mm, "end": v(-126.42, 38.85) * mm});
            skLineSegment(sketch, "E303", {"start": v(46.95, 53.8) * mm, "end": v(47.24, 57.2) * mm});
            skLineSegment(sketch, "E304", {"start": v(-123.86, 0) * mm, "end": v(-123.42, -0.44) * mm});
            skLineSegment(sketch, "E305", {"start": v(-123.86, 6.46) * mm, "end": v(-123.42, 7.5) * mm});
            skLineSegment(sketch, "E306", {"start": v(-123.86, 0) * mm, "end": v(-123.42, -1.5) * mm});
            skLineSegment(sketch, "E307", {"start": v(68.98, 78.95) * mm, "end": v(71.91, 78.76) * mm});
            skLineSegment(sketch, "E308", {"start": v(68.98, 124.5) * mm, "end": v(68.98, 124.94) * mm});
            skSolve(sketch);
        }
        {
            var Q0;
            Q0=makeQuery(id+"F0.imprint","IMPRINT",FACE,{"disambiguationData":[TD([[makeQuery(id+"F0.imprint","IMPRINT",EDGE,{"derivedFrom":sQuery(id+"F0.wireOp",EDGE,"E0")}),1.0]])]});
            var Q1;
            Q1=makeQuery(id+"F0.imprint","IMPRINT",FACE,{"disambiguationData":[TD([[makeQuery(id+"F0.imprint","IMPRINT",EDGE,{"derivedFrom":sQuery(id+"F0.wireOp",EDGE,"E143.MirrorCS")}),1.0]])]});
            var Q2;
            {var subQ6=sQuery(id+"F0.wireOp",EDGE,"E299");Q2=makeQuery(id+"F0.imprint","IMPRINT",FACE,{"disambiguationData":[TD([[makeQuery(id+"F0.imprint","IMPRINT",EDGE,{"derivedFrom":subQ6}),1.0]])]});}
            var Q3;
            {var subQ0=sQuery(id+"F0.wireOp",EDGE,"E282");Q3=makeQuery(id+"F0.imprint","IMPRINT",FACE,{"disambiguationData":[TD([[makeQuery(id+"F0.imprint","IMPRINT",EDGE,{"derivedFrom":subQ0}),-1.0]])]});}
            var Q4;
            {var subQ0=sQuery(id+"F0.wireOp",EDGE,"E283");Q4=makeQuery(id+"F0.imprint","IMPRINT",FACE,{"disambiguationData":[TD([[makeQuery(id+"F0.imprint","IMPRINT",EDGE,{"derivedFrom":subQ0}),1.0]])]});}
            var Q5;
            Q5=makeQuery(id+"F0.imprint","IMPRINT",FACE,{"disambiguationData":[TD([[makeQuery(id+"F0.imprint","IMPRINT",EDGE,{"derivedFrom":sQuery(id+"F0.wireOp",EDGE,"E128.MirrorCS")}),1.0]])]});
            var Q6;
            Q6=makeQuery(id+"F0.imprint","IMPRINT",FACE,{"disambiguationData":[TD([[makeQuery(id+"F0.imprint","IMPRINT",EDGE,{"derivedFrom":sQuery(id+"F0.wireOp",EDGE,"E280.MirrorCS")}),1.0]])]});
            var Q7;
            {var subQ0=sQuery(id+"F0.wireOp",EDGE,"E277.MirrorCS");var subQ1=sQuery(id+"F0.wireOp",EDGE,"E139");var subQ2=makeQuery(id+"F0.imprint","INTERSECT",VERTEX,{"derivedFrom":[subQ1,subQ0]});Q7=makeQuery(id+"F0.imprint","IMPRINT",FACE,{"disambiguationData":[TD([[makeQuery(id+"F0.imprint","IMPRINT",EDGE,{"disambiguationData":[TD([[subQ2,1.0]])],"derivedFrom":subQ1}),1.0]])]});}
            var Q8;
            Q8=makeQuery(id+"F0.imprint","IMPRINT",FACE,{"disambiguationData":[TD([[makeQuery(id+"F0.imprint","IMPRINT",EDGE,{"derivedFrom":sQuery(id+"F0.wireOp",EDGE,"E297")}),1.0]])]});
            extrude(context, id + "F1", {"entities" : qUnion([Q0, Q1, Q2, Q3, Q4, Q5, Q6, Q7, Q8]), "depth" : 15 * mm});
        }
        {
            var Q0;
            Q0=makeQuery(id+"F1.opExtrude","SWEPT_EDGE",EDGE,{"disambiguationData":[OSD([sQuery(id+"F0.wireOp",EDGE,"E284"),sQuery(id+"F0.wireOp",EDGE,"E285")])]});
            fillet(context, id + "F2", {"entities" : qUnion([Q0]), "radius" : 3 * mm, "tangentPropagation" : true, "allowEdgeOverflow" : false});
        }
    });
